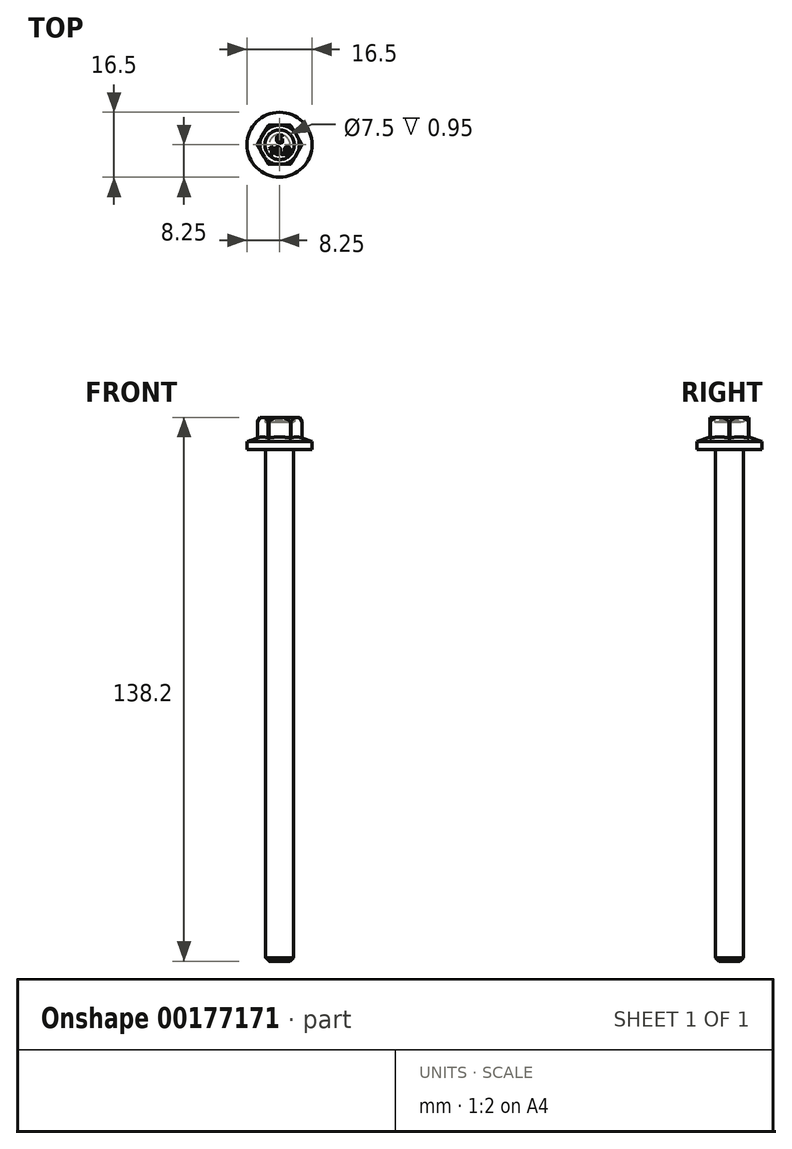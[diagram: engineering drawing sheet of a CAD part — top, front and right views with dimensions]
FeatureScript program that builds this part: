
annotation { "Feature Type Name" : "Feature", "Feature Type Description" : "" }
export const myFeature = defineFeature(function(context is Context, id is Id, definition is map)
    precondition{}
    {
        {
            var Q0;
            Q0=qCreatedBy(makeId("Front.planeOp"),FACE);
            var sketch = newSketch(context, id + "F0", { "sketchPlane" : qUnion([Q0])});
            skLineSegment(sketch, "E0", {"start": v(0, 0) * mm, "end": v(0, 7.05) * mm});
            skLineSegment(sketch, "E1", {"start": v(3.75, 8.2) * mm, "end": v(5.01, 8.2) * mm});
            skLineSegment(sketch, "E2", {"start": v(5.65, 7.1) * mm, "end": v(5.65, 2.95) * mm});
            skLineSegment(sketch, "E3", {"start": v(5.65, 2.95) * mm, "end": v(8.25, 2) * mm});
            skLineSegment(sketch, "E4", {"start": v(8.25, 2) * mm, "end": v(8.25, 0) * mm});
            skLineSegment(sketch, "E5", {"start": v(8.25, 0) * mm, "end": v(3.53, 0) * mm});
            skLineSegment(sketch, "E6", {"start": v(5.01, 8.2) * mm, "end": v(5.65, 7.1) * mm});
            skLineSegment(sketch, "E7", {"start": v(3.75, 8.2) * mm, "end": v(3.75, 7.25) * mm});
            skLineSegment(sketch, "E8", {"start": v(3.55, 7.05) * mm, "end": v(0, 7.05) * mm});
            skPoint(sketch, "E9.visualSharp", {"position": v(3.75, 7.05) * mm});
            skArc(sketch, "E9.filletArc", {"start": v(3.55, 7.05) * mm, "mid": v(3.7, 7.1) * mm, "end": v(3.75, 7.25) * mm});
            skLineSegment(sketch, "E10", {"start": v(0, 0) * mm, "end": v(0, -130) * mm});
            skLineSegment(sketch, "E11", {"start": v(0, -130) * mm, "end": v(2.65, -130) * mm});
            skLineSegment(sketch, "E12", {"start": v(2.65, -130) * mm, "end": v(3.54, -129.11) * mm});
            skLineSegment(sketch, "E13", {"start": v(3.54, -129.11) * mm, "end": v(3.53, 0) * mm});
            skSolve(sketch);
        }
        {
            var Q0;
            Q0=qSketchRegion(id+"F0",true);
            var Q1;
            Q1=sQuery(id+"F0.wireOp",EDGE,"E0");
            revolve(context, id + "F1", {"entities" : qUnion([Q0]), "axis" : qUnion([Q1]), "revolveType" : RevolveType.FULL});
        }
        {
            var Q0;
            Q0=makeQuery(id+"F1.opRevolve","SWEPT_FACE",FACE,{"disambiguationData":[OSD([sQuery(id+"F0.wireOp",EDGE,"E1")])]});
            var sketch = newSketch(context, id + "F2", { "sketchPlane" : qUnion([Q0])});
            skCircle(sketch, "E14.cCircle", {"center": v(0, 0) * mm, "radius": 4.95 * mm, "construction": true});
            skLineSegment(sketch, "E14.0", {"start": v(-2.86, 4.95) * mm, "end": v(2.86, 4.95) * mm});
            skLineSegment(sketch, "E14.1", {"start": v(2.86, 4.95) * mm, "end": v(5.72, 0) * mm});
            skLineSegment(sketch, "E14.2", {"start": v(5.72, 0) * mm, "end": v(2.86, -4.95) * mm});
            skLineSegment(sketch, "E14.3", {"start": v(2.86, -4.95) * mm, "end": v(-2.86, -4.95) * mm});
            skLineSegment(sketch, "E14.4", {"start": v(-2.86, -4.95) * mm, "end": v(-5.72, 0) * mm});
            skLineSegment(sketch, "E14.5", {"start": v(-5.72, 0) * mm, "end": v(-2.86, 4.95) * mm});
            skPoint(sketch, "E14.0.midPoint", {"position": v(0, 4.95) * mm});
            skCircle(sketch, "E15", {"center": v(0, 0) * mm, "radius": 9.6 * mm});
            skSolve(sketch);
        }
        {
            var Q0;
            Q0=qSketchRegion(id+"F2",true);
            var Q1;
            Q1=makeQuery(id+"F1.opRevolve","SWEPT_FACE",FACE,{"disambiguationData":[OSD([sQuery(id+"F0.wireOp",EDGE,"E3")])]});
            extrude(context, id + "F3", {"entities" : qUnion([Q0]), "operationType" : NewBodyOperationType.REMOVE, "endBound" : BoundingType.UP_TO_SURFACE, "oppositeDirection" : true, "endBoundEntityFace" : qUnion([Q1]), "depth" : 25 * mm});
        }
        {
            var Q0;
            Q0=makeQuery(id+"F1.opRevolve","SWEPT_FACE",FACE,{"disambiguationData":[OSD([sQuery(id+"F0.wireOp",EDGE,"E8")])]});
            var sketch = newSketch(context, id + "F4", { "sketchPlane" : qUnion([Q0])});
            skText(sketch, "E16", { "text": "G", "fontName": "OpenSans-Bold.ttf"});
            skText(sketch, "E17", { "text": "10.9", "fontName": "OpenSans-Bold.ttf"});
            const initialGuessF4  = {"E16": [-0.00098, 0.0005, 1, 0, 0.002], "E17": [-0.00282, -0.0025, 1, 0, 0.002]};
            skSetInitialGuess(sketch, initialGuessF4);
            skSolve(sketch);
        }
        {
            var Q0;
            Q0 = qSketchRegion(id + "F4", true);
            extrude(context, id + "F5", {"entities" : qUnion([Q0]), "operationType" : NewBodyOperationType.ADD, "depth" : 0.3 * mm, "hasDraft" : true, "draftAngle" : 12 * degree, "draftPullDirection" : true});
        }
    });
